# Revit family: Bathtub_Contemporary_Pacifica_ABA904R_TOTO
name_source: partatom
category: Plumbing Fixtures
revit_build: Autodesk Revit Architecture 2013 (Build: 20130531_2115(x64)
units: mm (PartAtom-declared; Revit-internal decimal feet)

## types (1)
- ABA904R
    04 CSI = 22 41 19
    95 CSI = 15410
    Apparent Power = 0 VA
    Assembly Code = D2010510
    Blower Motor Power = 746 W
    Bottom Plate = Metal - TOTO - LifeKoat - Brass - Polished
    CAD Drawing URL = http://www.totousa.com
    Color Availability = #01  Cotton, #12  Sedona Beige
    Default Elevation = 48"
    Depth = 72"
    Description = Air Bathtub
    Finish = Metal - TOTO - Chrome - Polished
    Frequency = 60 Hz
    Full Load Amps = 15 A
    Height = 2 7/8"
    Industry Standards = 1800 VA
    Manufacturer = TOTO USA, Inc.
    Manufacturer Fax = (770) 282-0002
    Model = ABA904R
    Number of Poles = 1
    Phase = 1
    Series = Pacifica
    Shipping Weight = 150.00 lb
    Spec Sheet URL = http://www.totousa.com
    Style = Contemporary
    Subcategory = Bathtubs
    Toto BIM Number = BM-00159
    URL = http://www.totousa.com
    Voltage = 120 V
    Warranty = 1 Year Limited Warranty on acrylic tub; 1 Year Limited Warranty on components and parts
    Warranty URL = http://www.totousa.com
    Waste Connection NPT = 2"
    Waste Connection Radius = 1"
    Width = 42"

## geometry (parser evidence)
native form markers: Blend x24, Sweep x3
no freeform markers — native parametric forms only
